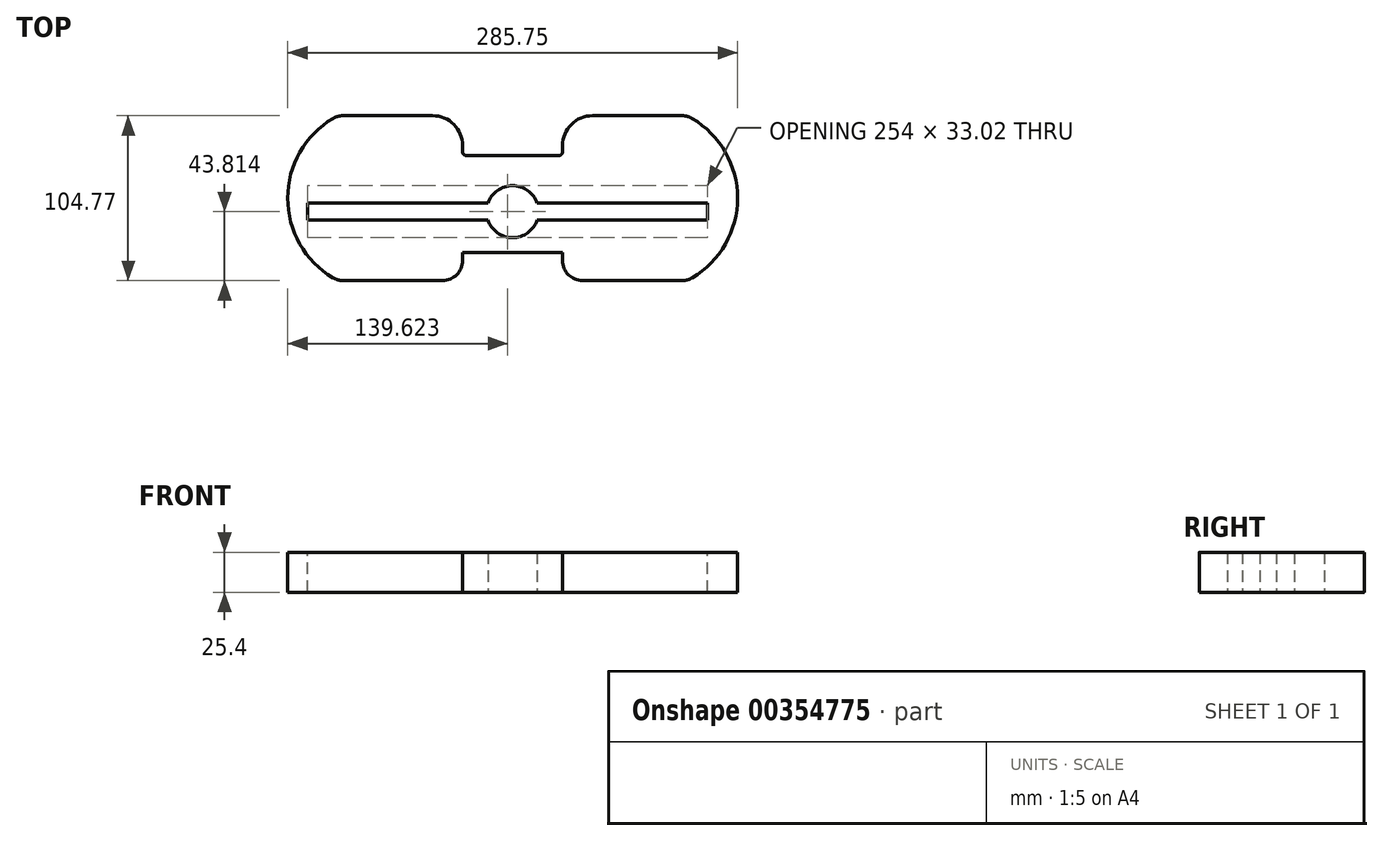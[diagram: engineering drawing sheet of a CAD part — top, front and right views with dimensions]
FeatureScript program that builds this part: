
annotation { "Feature Type Name" : "Feature", "Feature Type Description" : "" }
export const myFeature = defineFeature(function(context is Context, id is Id, definition is map)
    precondition{}
    {
        {
            var Q0;
            Q0=qCreatedBy(makeId("Top.planeOp"),FACE);
            var sketch = newSketch(context, id + "F0", { "sketchPlane" : qUnion([Q0])});
            skLineSegment(sketch, "E0", {"start": v(-116.27, 49.9) * mm, "end": v(-59.47, 49.9) * mm});
            skLineSegment(sketch, "E1", {"start": v(-53.12, -54.87) * mm, "end": v(-116.27, -54.87) * mm});
            skLineSegment(sketch, "E2", {"start": v(-37.88, 24.5) * mm, "end": v(-8.67, 24.5) * mm});
            skLineSegment(sketch, "E3", {"start": v(-40.42, -37.1) * mm, "end": v(-8.67, -37.1) * mm});
            skLineSegment(sketch, "E4", {"start": v(-40.42, 30.85) * mm, "end": v(-40.42, 27.04) * mm});
            skLineSegment(sketch, "E5", {"start": v(-40.42, 24.5) * mm, "end": v(-40.42, -37.1) * mm});
            skLineSegment(sketch, "E6", {"start": v(-40.42, -37.1) * mm, "end": v(-40.42, -42.17) * mm});
            skArc(sketch, "E7", {"start": v(-122.76, 48.12) * mm, "mid": v(-151.55, -2.48) * mm, "end": v(-122.76, -53.09) * mm});
            skLineSegment(sketch, "E8.MirrorCS", {"start": v(23.08, -37.1) * mm, "end": v(23.08, -42.17) * mm});
            skLineSegment(sketch, "E9.MirrorCS", {"start": v(23.08, 30.85) * mm, "end": v(23.08, 27.04) * mm});
            skLineSegment(sketch, "E10.MirrorCS", {"start": v(35.78, -54.87) * mm, "end": v(98.92, -54.87) * mm});
            skLineSegment(sketch, "E11.MirrorCS", {"start": v(23.08, 24.5) * mm, "end": v(23.08, -37.1) * mm});
            skArc(sketch, "E12.MirrorCS", {"start": v(105.41, 48.12) * mm, "mid": v(134.2, -2.48) * mm, "end": v(105.41, -53.09) * mm});
            skLineSegment(sketch, "E13.MirrorCS", {"start": v(23.08, -37.1) * mm, "end": v(-8.67, -37.1) * mm});
            skLineSegment(sketch, "E14.MirrorCS", {"start": v(20.54, 24.5) * mm, "end": v(-8.67, 24.5) * mm});
            skPoint(sketch, "E15.visualSharp", {"position": v(-40.42, 49.9) * mm});
            skArc(sketch, "E15.filletArc", {"start": v(-40.42, 30.85) * mm, "mid": v(-46, 44.32) * mm, "end": v(-59.47, 49.9) * mm});
            skPoint(sketch, "E16.newPointA", {"position": v(23.08, 49.9) * mm});
            skArc(sketch, "E16.filletArc", {"start": v(42.13, 49.9) * mm, "mid": v(28.66, 44.32) * mm, "end": v(23.08, 30.85) * mm});
            skPoint(sketch, "E17.visualSharp", {"position": v(-40.42, -54.87) * mm});
            skArc(sketch, "E17.filletArc", {"start": v(-53.12, -54.87) * mm, "mid": v(-44.14, -51.15) * mm, "end": v(-40.42, -42.17) * mm});
            skPoint(sketch, "E18.visualSharp", {"position": v(23.08, -54.87) * mm});
            skArc(sketch, "E18.filletArc", {"start": v(23.08, -42.17) * mm, "mid": v(26.8, -51.15) * mm, "end": v(35.78, -54.87) * mm});
            skLineSegment(sketch, "E19", {"start": v(42.13, 49.9) * mm, "end": v(98.92, 49.9) * mm});
            skPoint(sketch, "E20.visualSharp", {"position": v(-119.54, 49.9) * mm});
            skArc(sketch, "E20.filletArc", {"start": v(-116.27, 49.9) * mm, "mid": v(-119.64, 49.45) * mm, "end": v(-122.76, 48.12) * mm});
            skPoint(sketch, "E21.visualSharp", {"position": v(-119.54, -54.87) * mm});
            skArc(sketch, "E21.filletArc", {"start": v(-122.76, -53.09) * mm, "mid": v(-119.64, -54.42) * mm, "end": v(-116.27, -54.87) * mm});
            skPoint(sketch, "E22.visualSharp", {"position": v(102.19, -54.87) * mm});
            skArc(sketch, "E22.filletArc", {"start": v(98.92, -54.87) * mm, "mid": v(102.29, -54.42) * mm, "end": v(105.41, -53.09) * mm});
            skPoint(sketch, "E23.visualSharp", {"position": v(102.19, 49.9) * mm});
            skArc(sketch, "E23.filletArc", {"start": v(105.41, 48.12) * mm, "mid": v(102.29, 49.45) * mm, "end": v(98.92, 49.9) * mm});
            skCircle(sketch, "E24", {"center": v(-8.67, -11.06) * mm, "radius": 16.51 * mm});
            skPoint(sketch, "E25.visualSharp", {"position": v(-40.42, 24.5) * mm});
            skArc(sketch, "E25.filletArc", {"start": v(-40.42, 27.04) * mm, "mid": v(-39.68, 25.25) * mm, "end": v(-37.88, 24.5) * mm});
            skPoint(sketch, "E26.visualSharp", {"position": v(23.08, 24.5) * mm});
            skArc(sketch, "E26.filletArc", {"start": v(20.54, 24.5) * mm, "mid": v(22.33, 25.25) * mm, "end": v(23.08, 27.04) * mm});
            skSolve(sketch);
        }
        {
            var Q0;
            Q0 = qSketchRegion(id + "F0", true);
            extrude(context, id + "F1", {"entities" : qUnion([Q0]), "depth" : 25.4 * mm});
        }
        {
            var Q0;
            Q0=makeQuery(id+"F1.opExtrude","CAP_FACE",FACE,{"disambiguationData":[OSD([sQuery(id+"F0.wireOp",EDGE,"E0"),sQuery(id+"F0.wireOp",EDGE,"E1"),sQuery(id+"F0.wireOp",EDGE,"E2"),sQuery(id+"F0.wireOp",EDGE,"E3"),sQuery(id+"F0.wireOp",EDGE,"E4"),sQuery(id+"F0.wireOp",EDGE,"E6"),sQuery(id+"F0.wireOp",EDGE,"E7"),sQuery(id+"F0.wireOp",EDGE,"E8.MirrorCS"),sQuery(id+"F0.wireOp",EDGE,"E9.MirrorCS"),sQuery(id+"F0.wireOp",EDGE,"E10.MirrorCS"),sQuery(id+"F0.wireOp",EDGE,"E12.MirrorCS"),sQuery(id+"F0.wireOp",EDGE,"E13.MirrorCS"),sQuery(id+"F0.wireOp",EDGE,"E14.MirrorCS"),sQuery(id+"F0.wireOp",EDGE,"E15.filletArc"),sQuery(id+"F0.wireOp",EDGE,"E16.filletArc"),sQuery(id+"F0.wireOp",EDGE,"E17.filletArc"),sQuery(id+"F0.wireOp",EDGE,"E18.filletArc"),sQuery(id+"F0.wireOp",EDGE,"E19"),sQuery(id+"F0.wireOp",EDGE,"E20.filletArc"),sQuery(id+"F0.wireOp",EDGE,"E21.filletArc"),sQuery(id+"F0.wireOp",EDGE,"E22.filletArc"),sQuery(id+"F0.wireOp",EDGE,"E23.filletArc"),sQuery(id+"F0.wireOp",EDGE,"E24"),sQuery(id+"F0.wireOp",EDGE,"E25.filletArc"),sQuery(id+"F0.wireOp",EDGE,"E26.filletArc")])],"isStart":false});
            var sketch = newSketch(context, id + "F2", { "sketchPlane" : qUnion([Q0])});
            skLineSegment(sketch, "E27.bottom", {"start": v(-138.93, -5.72) * mm, "end": v(115.07, -5.72) * mm});
            skLineSegment(sketch, "E27.top", {"start": v(-138.93, -16.39) * mm, "end": v(115.07, -16.39) * mm});
            skLineSegment(sketch, "E27.left", {"start": v(-138.93, -5.72) * mm, "end": v(-138.93, -16.39) * mm});
            skLineSegment(sketch, "E27.right", {"start": v(115.07, -5.72) * mm, "end": v(115.07, -16.39) * mm});
            skSolve(sketch);
        }
        {
            var Q0;
            {var subQ0=sQuery(id+"F2.wireOp",EDGE,"E27.right");Q0=makeQuery(id+"F2.imprint","IMPRINT",FACE,{"disambiguationData":[TD([[makeQuery(id+"F2.imprint","IMPRINT",EDGE,{"derivedFrom":subQ0}),-1.0]])]});}
            var Q1;
            {var subQ0=sQuery(id+"F2.wireOp",EDGE,"E27.bottom");var subQ1=makeQuery(id+"F1.opExtrude","CAP_EDGE",EDGE,{"disambiguationData":[OSD([sQuery(id+"F0.wireOp",EDGE,"E24")])],"isStart":false});var subQ2=makeQuery(id+"F2.imprint","INTERSECT",VERTEX,{"disambiguationData":[OD(0.0)],"derivedFrom":[subQ1,subQ0]});Q1=makeQuery(id+"F2.imprint","IMPRINT",FACE,{"disambiguationData":[TD([[makeQuery(id+"F2.imprint","IMPRINT",EDGE,{"disambiguationData":[TD([[subQ2,-1.0]])],"derivedFrom":subQ0}),-1.0]])]});}
            var Q2;
            {var subQ0=sQuery(id+"F2.wireOp",EDGE,"E27.left");Q2=makeQuery(id+"F2.imprint","IMPRINT",FACE,{"disambiguationData":[TD([[makeQuery(id+"F2.imprint","IMPRINT",EDGE,{"derivedFrom":subQ0}),1.0]])]});}
            extrude(context, id + "F3", {"entities" : qUnion([Q0, Q1, Q2]), "operationType" : NewBodyOperationType.REMOVE, "oppositeDirection" : true, "depth" : 25.4 * mm});
        }
    });
